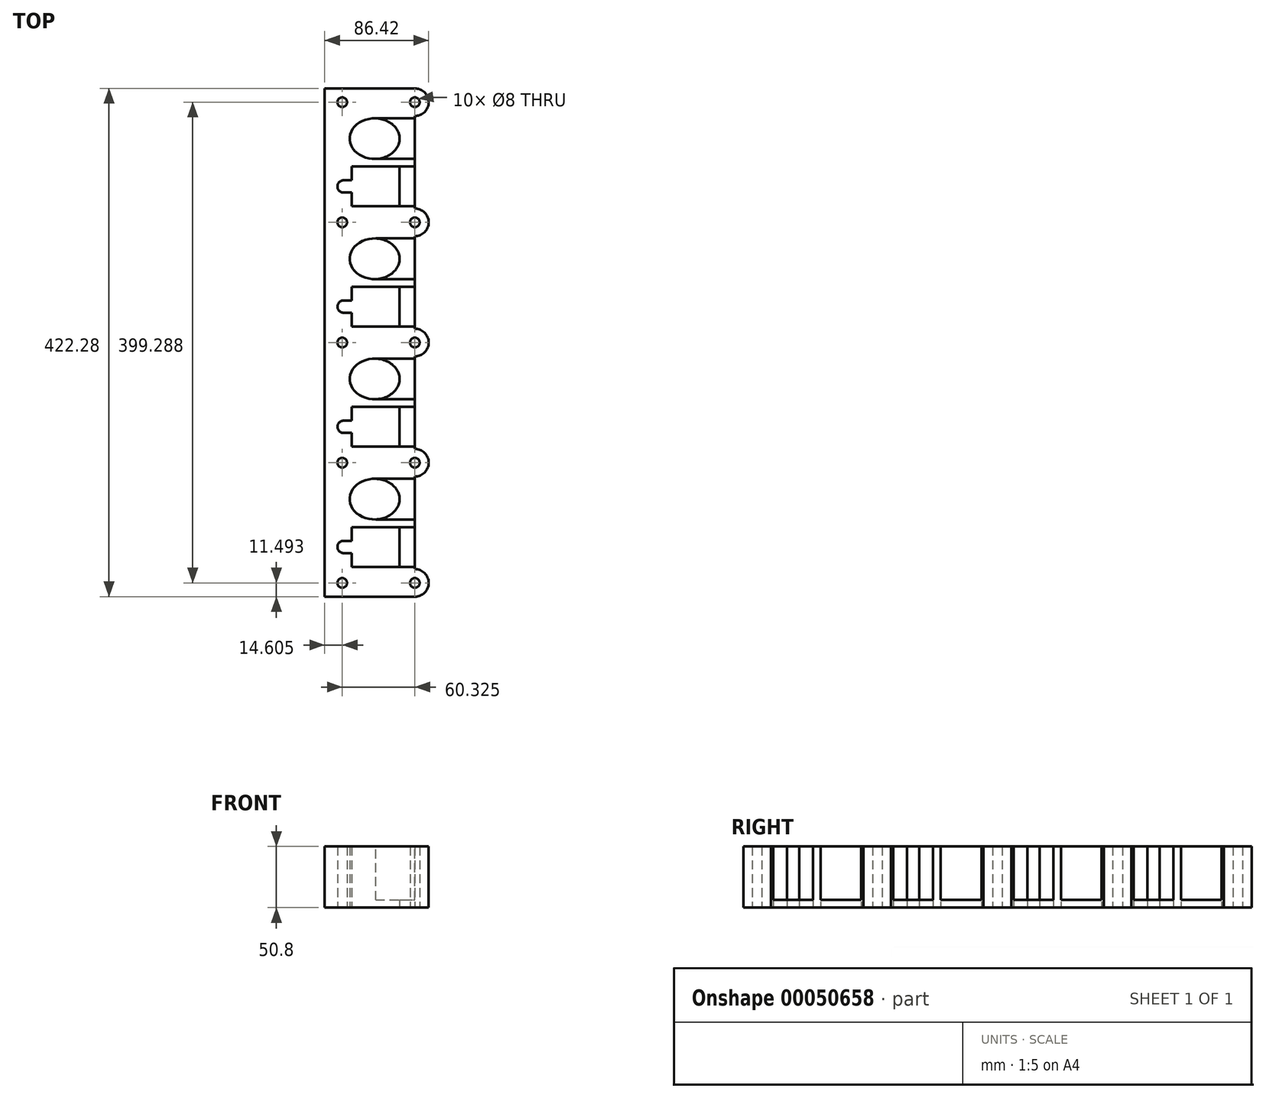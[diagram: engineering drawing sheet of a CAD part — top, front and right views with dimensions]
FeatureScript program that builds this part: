
annotation { "Feature Type Name" : "Feature", "Feature Type Description" : "" }
export const myFeature = defineFeature(function(context is Context, id is Id, definition is map)
    precondition{}
    {
        {
            var Q0;
            Q0=qCreatedBy(makeId("Top.planeOp"),FACE);
            var sketch = newSketch(context, id + "F0", { "sketchPlane" : qUnion([Q0])});
            skLineSegment(sketch, "E0.bottom", {"start": v(-7.62, 422.27) * mm, "end": v(-82.55, 422.27) * mm});
            skLineSegment(sketch, "E0.top", {"start": v(-7.62, 0) * mm, "end": v(-82.55, 0) * mm});
            skLineSegment(sketch, "E0.right", {"start": v(-82.55, 422.28) * mm, "end": v(-82.55, 0) * mm});
            skEllipse(sketch, "E1", {"center": v(-41.02, 81.09) * mm, "majorRadius": 20.7 * mm, "minorRadius": 16.9 * mm, "majorAxis": v(1, 0)});
            skLineSegment(sketch, "E2.bottom", {"start": v(-20.32, 57.85) * mm, "end": v(-59.94, 57.85) * mm});
            skLineSegment(sketch, "E2.top", {"start": v(-20.32, 24.83) * mm, "end": v(-59.94, 24.83) * mm});
            skLineSegment(sketch, "E2.left", {"start": v(-20.32, 57.85) * mm, "end": v(-20.32, 24.83) * mm});
            skLineSegment(sketch, "E2.right", {"start": v(-59.94, 57.85) * mm, "end": v(-59.94, 46.42) * mm});
            skLineSegment(sketch, "E3.bottom", {"start": v(-59.94, 46.42) * mm, "end": v(-66.8, 46.42) * mm});
            skLineSegment(sketch, "E3.top", {"start": v(-59.94, 36.26) * mm, "end": v(-66.8, 36.26) * mm});
            skArc(sketch, "E4", {"start": v(-66.8, 46.42) * mm, "mid": v(-71.88, 41.34) * mm, "end": v(-66.8, 36.26) * mm});
            skLineSegment(sketch, "E5.trimOffspring", {"start": v(-59.94, 36.26) * mm, "end": v(-59.94, 24.83) * mm});
            skPoint(sketch, "E6", {"position": v(-41.02, 64.2) * mm});
            skPoint(sketch, "E7", {"position": v(-20.32, 81.09) * mm});
            skPoint(sketch, "E8", {"position": v(-41.02, 97.98) * mm});
            skPoint(sketch, "E9.0.1.0", {"position": v(-41.02, 164.02) * mm});
            skPoint(sketch, "E9.0.1.1", {"position": v(-20.32, 180.91) * mm});
            skLineSegment(sketch, "E9.0.1.2", {"start": v(-20.32, 157.67) * mm, "end": v(-20.32, 124.65) * mm});
            skPoint(sketch, "E9.0.1.3", {"position": v(-41.02, 197.8) * mm});
            skLineSegment(sketch, "E9.0.1.4", {"start": v(-59.94, 136.08) * mm, "end": v(-66.8, 136.08) * mm});
            skLineSegment(sketch, "E9.0.1.5", {"start": v(-59.94, 157.67) * mm, "end": v(-59.94, 146.24) * mm});
            skLineSegment(sketch, "E9.0.1.6", {"start": v(-59.94, 146.24) * mm, "end": v(-66.8, 146.24) * mm});
            skEllipse(sketch, "E9.0.1.7", {"center": v(-41.02, 180.91) * mm, "majorRadius": 20.7 * mm, "minorRadius": 16.9 * mm, "majorAxis": v(1, 0)});
            skLineSegment(sketch, "E9.0.1.8", {"start": v(-59.94, 136.08) * mm, "end": v(-59.94, 124.65) * mm});
            skLineSegment(sketch, "E9.0.1.9", {"start": v(-20.32, 124.65) * mm, "end": v(-59.94, 124.65) * mm});
            skLineSegment(sketch, "E9.0.1.10", {"start": v(-20.32, 157.67) * mm, "end": v(-59.94, 157.67) * mm});
            skArc(sketch, "E9.0.1.11", {"start": v(-66.8, 146.24) * mm, "mid": v(-71.88, 141.16) * mm, "end": v(-66.8, 136.08) * mm});
            skPoint(sketch, "E9.0.2.0", {"position": v(-41.02, 263.84) * mm});
            skPoint(sketch, "E9.0.2.1", {"position": v(-20.32, 280.73) * mm});
            skLineSegment(sketch, "E9.0.2.2", {"start": v(-20.32, 257.5) * mm, "end": v(-20.32, 224.47) * mm});
            skPoint(sketch, "E9.0.2.3", {"position": v(-41.02, 297.62) * mm});
            skLineSegment(sketch, "E9.0.2.4", {"start": v(-59.94, 235.9) * mm, "end": v(-66.8, 235.9) * mm});
            skLineSegment(sketch, "E9.0.2.5", {"start": v(-59.94, 257.5) * mm, "end": v(-59.94, 246.06) * mm});
            skLineSegment(sketch, "E9.0.2.6", {"start": v(-59.94, 246.06) * mm, "end": v(-66.8, 246.06) * mm});
            skEllipse(sketch, "E9.0.2.7", {"center": v(-41.02, 280.73) * mm, "majorRadius": 20.7 * mm, "minorRadius": 16.9 * mm, "majorAxis": v(1, 0)});
            skLineSegment(sketch, "E9.0.2.8", {"start": v(-59.94, 235.9) * mm, "end": v(-59.94, 224.47) * mm});
            skLineSegment(sketch, "E9.0.2.9", {"start": v(-20.32, 224.47) * mm, "end": v(-59.94, 224.47) * mm});
            skLineSegment(sketch, "E9.0.2.10", {"start": v(-20.32, 257.5) * mm, "end": v(-59.94, 257.5) * mm});
            skArc(sketch, "E9.0.2.11", {"start": v(-66.8, 246.06) * mm, "mid": v(-71.88, 240.98) * mm, "end": v(-66.8, 235.9) * mm});
            skPoint(sketch, "E9.0.3.0", {"position": v(-41.02, 363.66) * mm});
            skPoint(sketch, "E9.0.3.1", {"position": v(-20.32, 380.56) * mm});
            skLineSegment(sketch, "E9.0.3.2", {"start": v(-20.32, 357.31) * mm, "end": v(-20.32, 324.3) * mm});
            skPoint(sketch, "E9.0.3.3", {"position": v(-41.02, 397.45) * mm});
            skLineSegment(sketch, "E9.0.3.4", {"start": v(-59.94, 335.72) * mm, "end": v(-66.8, 335.72) * mm});
            skLineSegment(sketch, "E9.0.3.5", {"start": v(-59.94, 357.31) * mm, "end": v(-59.94, 345.88) * mm});
            skLineSegment(sketch, "E9.0.3.6", {"start": v(-59.94, 345.88) * mm, "end": v(-66.8, 345.88) * mm});
            skEllipse(sketch, "E9.0.3.7", {"center": v(-41.02, 380.56) * mm, "majorRadius": 20.7 * mm, "minorRadius": 16.9 * mm, "majorAxis": v(1, 0)});
            skLineSegment(sketch, "E9.0.3.8", {"start": v(-59.94, 335.72) * mm, "end": v(-59.94, 324.3) * mm});
            skLineSegment(sketch, "E9.0.3.9", {"start": v(-20.32, 324.3) * mm, "end": v(-59.94, 324.3) * mm});
            skLineSegment(sketch, "E9.0.3.10", {"start": v(-20.32, 357.31) * mm, "end": v(-59.94, 357.31) * mm});
            skArc(sketch, "E9.0.3.11", {"start": v(-66.8, 345.88) * mm, "mid": v(-71.88, 340.8) * mm, "end": v(-66.8, 335.72) * mm});
            skLineSegment(sketch, "E9.direction1", {"start": v(-41.02, 64.2) * mm, "end": v(-15.62, 64.2) * mm, "construction": true});
            skLineSegment(sketch, "E9.direction2", {"start": v(-41.02, 64.2) * mm, "end": v(-41.02, 164.02) * mm, "construction": true});
            skLineSegment(sketch, "E10", {"start": v(-82.55, 11.5) * mm, "end": v(-19.11, 11.5) * mm, "construction": true});
            skLineSegment(sketch, "E11", {"start": v(-7.62, 11.5) * mm, "end": v(-7.62, 15.5) * mm, "construction": true});
            skLineSegment(sketch, "E12", {"start": v(-67.94, 422.27) * mm, "end": v(-67.94, 11.5) * mm, "construction": true});
            skLineSegment(sketch, "E13", {"start": v(-82.55, 364.1) * mm, "end": v(0, 364.1) * mm, "construction": true});
            skCircle(sketch, "E14", {"center": v(-7.62, 11.5) * mm, "radius": 4 * mm});
            skCircle(sketch, "E15", {"center": v(-67.94, 11.5) * mm, "radius": 4 * mm});
            skArc(sketch, "E16", {"start": v(-7.62, 0) * mm, "mid": v(3.87, 11.5) * mm, "end": v(-7.62, 22.99) * mm});
            skArc(sketch, "E17.0.1.0", {"start": v(-7.62, 99.82) * mm, "mid": v(3.87, 111.32) * mm, "end": v(-7.62, 122.8) * mm});
            skCircle(sketch, "E17.0.1.1", {"center": v(-7.62, 111.32) * mm, "radius": 4 * mm});
            skCircle(sketch, "E17.0.1.2", {"center": v(-67.94, 111.32) * mm, "radius": 4 * mm});
            skArc(sketch, "E17.0.2.0", {"start": v(-7.62, 199.64) * mm, "mid": v(3.87, 211.14) * mm, "end": v(-7.62, 222.63) * mm});
            skCircle(sketch, "E17.0.2.1", {"center": v(-7.62, 211.14) * mm, "radius": 4 * mm});
            skCircle(sketch, "E17.0.2.2", {"center": v(-67.94, 211.14) * mm, "radius": 4 * mm});
            skArc(sketch, "E17.0.3.0", {"start": v(-7.62, 299.47) * mm, "mid": v(3.87, 310.96) * mm, "end": v(-7.62, 322.45) * mm});
            skCircle(sketch, "E17.0.3.1", {"center": v(-7.62, 310.96) * mm, "radius": 4 * mm});
            skCircle(sketch, "E17.0.3.2", {"center": v(-67.94, 310.96) * mm, "radius": 4 * mm});
            skArc(sketch, "E17.0.4.0", {"start": v(-7.62, 399.29) * mm, "mid": v(3.87, 410.78) * mm, "end": v(-7.62, 422.27) * mm});
            skCircle(sketch, "E17.0.4.1", {"center": v(-7.62, 410.78) * mm, "radius": 4 * mm});
            skCircle(sketch, "E17.0.4.2", {"center": v(-67.94, 410.78) * mm, "radius": 4 * mm});
            skLineSegment(sketch, "E17.direction1", {"start": v(-7.62, 11.5) * mm, "end": v(11.43, 11.5) * mm, "construction": true});
            skLineSegment(sketch, "E18", {"start": v(-7.62, 399.29) * mm, "end": v(-7.62, 322.45) * mm});
            skLineSegment(sketch, "E19", {"start": v(-7.62, 222.63) * mm, "end": v(-7.62, 299.47) * mm});
            skLineSegment(sketch, "E20", {"start": v(-7.62, 199.64) * mm, "end": v(-7.62, 122.8) * mm});
            skLineSegment(sketch, "E21", {"start": v(-7.62, 99.82) * mm, "end": v(-7.62, 22.99) * mm});
            skLineSegment(sketch, "E22.trimOffspring", {"start": v(-7.62, 122.8) * mm, "end": v(-7.62, 422.27) * mm, "construction": true});
            skLineSegment(sketch, "E23.trimOffspring", {"start": v(0, 11.5) * mm, "end": v(0, 0) * mm});
            skLineSegment(sketch, "E24.trimOffspring", {"start": v(-7.62, 22.99) * mm, "end": v(-7.62, 99.82) * mm, "construction": true});
            skLineSegment(sketch, "E25.trimOffspring", {"start": v(-11.62, 11.5) * mm, "end": v(0, 11.5) * mm, "construction": true});
            skPoint(sketch, "E26.orphan", {"position": v(0, 422.28) * mm});
            skSolve(sketch);
        }
        {
            var Q0;
            Q0=makeQuery(id+"F0.imprint","IMPRINT",FACE,{"disambiguationData":[TD([[makeQuery(id+"F0.imprint","IMPRINT",EDGE,{"derivedFrom":sQuery(id+"F0.wireOp",EDGE,"E0.bottom")}),1.0]])]});
            extrude(context, id + "F1", {"entities" : qUnion([Q0]), "depth" : 50.8 * mm});
        }
        {
            var Q0;
            Q0=makeQuery(id+"F1.opExtrude","CAP_FACE",FACE,{"disambiguationData":[OSD([sQuery(id+"F0.wireOp",EDGE,"E0.bottom"),sQuery(id+"F0.wireOp",EDGE,"E0.top"),sQuery(id+"F0.wireOp",EDGE,"E0.right"),sQuery(id+"F0.wireOp",EDGE,"E1"),sQuery(id+"F0.wireOp",EDGE,"E2.bottom"),sQuery(id+"F0.wireOp",EDGE,"E2.top"),sQuery(id+"F0.wireOp",EDGE,"E2.left"),sQuery(id+"F0.wireOp",EDGE,"E2.right"),sQuery(id+"F0.wireOp",EDGE,"E3.bottom"),sQuery(id+"F0.wireOp",EDGE,"E3.top"),sQuery(id+"F0.wireOp",EDGE,"E4"),sQuery(id+"F0.wireOp",EDGE,"E5.trimOffspring"),sQuery(id+"F0.wireOp",EDGE,"E9.0.1.2"),sQuery(id+"F0.wireOp",EDGE,"E9.0.1.4"),sQuery(id+"F0.wireOp",EDGE,"E9.0.1.5"),sQuery(id+"F0.wireOp",EDGE,"E9.0.1.6"),sQuery(id+"F0.wireOp",EDGE,"E9.0.1.7"),sQuery(id+"F0.wireOp",EDGE,"E9.0.1.8"),sQuery(id+"F0.wireOp",EDGE,"E9.0.1.9"),sQuery(id+"F0.wireOp",EDGE,"E9.0.1.10"),sQuery(id+"F0.wireOp",EDGE,"E9.0.1.11"),sQuery(id+"F0.wireOp",EDGE,"E9.0.2.2"),sQuery(id+"F0.wireOp",EDGE,"E9.0.2.4"),sQuery(id+"F0.wireOp",EDGE,"E9.0.2.5"),sQuery(id+"F0.wireOp",EDGE,"E9.0.2.6"),sQuery(id+"F0.wireOp",EDGE,"E9.0.2.7"),sQuery(id+"F0.wireOp",EDGE,"E9.0.2.8"),sQuery(id+"F0.wireOp",EDGE,"E9.0.2.9"),sQuery(id+"F0.wireOp",EDGE,"E9.0.2.10"),sQuery(id+"F0.wireOp",EDGE,"E9.0.2.11"),sQuery(id+"F0.wireOp",EDGE,"E9.0.3.2"),sQuery(id+"F0.wireOp",EDGE,"E9.0.3.4"),sQuery(id+"F0.wireOp",EDGE,"E9.0.3.5"),sQuery(id+"F0.wireOp",EDGE,"E9.0.3.6"),sQuery(id+"F0.wireOp",EDGE,"E9.0.3.7"),sQuery(id+"F0.wireOp",EDGE,"E9.0.3.8"),sQuery(id+"F0.wireOp",EDGE,"E9.0.3.9"),sQuery(id+"F0.wireOp",EDGE,"E9.0.3.10"),sQuery(id+"F0.wireOp",EDGE,"E9.0.3.11"),sQuery(id+"F0.wireOp",EDGE,"E14"),sQuery(id+"F0.wireOp",EDGE,"E15"),sQuery(id+"F0.wireOp",EDGE,"E16"),sQuery(id+"F0.wireOp",EDGE,"E17.0.1.0"),sQuery(id+"F0.wireOp",EDGE,"E17.0.1.1"),sQuery(id+"F0.wireOp",EDGE,"E17.0.1.2"),sQuery(id+"F0.wireOp",EDGE,"E17.0.2.0"),sQuery(id+"F0.wireOp",EDGE,"E17.0.2.1"),sQuery(id+"F0.wireOp",EDGE,"E17.0.2.2"),sQuery(id+"F0.wireOp",EDGE,"E17.0.3.0"),sQuery(id+"F0.wireOp",EDGE,"E17.0.3.1"),sQuery(id+"F0.wireOp",EDGE,"E17.0.3.2"),sQuery(id+"F0.wireOp",EDGE,"E17.0.4.0"),sQuery(id+"F0.wireOp",EDGE,"E17.0.4.1"),sQuery(id+"F0.wireOp",EDGE,"E17.0.4.2"),sQuery(id+"F0.wireOp",EDGE,"E18"),sQuery(id+"F0.wireOp",EDGE,"E19"),sQuery(id+"F0.wireOp",EDGE,"E20"),sQuery(id+"F0.wireOp",EDGE,"E21")])],"isStart":false});
            var sketch = newSketch(context, id + "F2", { "sketchPlane" : qUnion([Q0])});
            skCircle(sketch, "E27", {"center": v(-66.8, 41.34) * mm, "radius": 12.7 * mm});
            skCircle(sketch, "E28", {"center": v(-66.8, 141.16) * mm, "radius": 12.7 * mm});
            skCircle(sketch, "E29", {"center": v(-66.8, 240.98) * mm, "radius": 12.7 * mm});
            skCircle(sketch, "E30", {"center": v(-66.8, 340.8) * mm, "radius": 12.7 * mm});
            skSolve(sketch);
        }
        {
            var Q0;
            Q0=makeQuery(id+"F2.imprint","IMPRINT",FACE,{"disambiguationData":[TD([[makeQuery(id+"F2.imprint","IMPRINT",EDGE,{"derivedFrom":makeQuery(id+"F1.opExtrude","CAP_EDGE",EDGE,{"disambiguationData":[OSD([sQuery(id+"F0.wireOp",EDGE,"E0.bottom")])],"isStart":false})}),1.0]])]});
            var sketch = newSketch(context, id + "F3", { "sketchPlane" : qUnion([Q0])});
            skPoint(sketch, "E31", {"position": v(-40.13, 97.96) * mm});
            skPoint(sketch, "E32", {"position": v(-40.13, 64.21) * mm});
            skPoint(sketch, "E33", {"position": v(-40.13, 57.85) * mm});
            skLineSegment(sketch, "E34", {"start": v(-40.13, 57.85) * mm, "end": v(-40.13, 99.27) * mm, "construction": true});
            skLineSegment(sketch, "E35.bottom", {"start": v(-40.13, 97.96) * mm, "end": v(-7.62, 97.96) * mm});
            skLineSegment(sketch, "E35.top", {"start": v(-40.13, 64.21) * mm, "end": v(-7.62, 64.21) * mm});
            skLineSegment(sketch, "E35.left", {"start": v(-40.13, 97.96) * mm, "end": v(-40.13, 64.21) * mm});
            skLineSegment(sketch, "E35.right", {"start": v(-7.62, 97.96) * mm, "end": v(-7.62, 64.21) * mm});
            skLineSegment(sketch, "E36.bottom", {"start": v(-40.13, 57.85) * mm, "end": v(-7.62, 57.85) * mm});
            skLineSegment(sketch, "E36.top", {"start": v(-40.13, 24.83) * mm, "end": v(-7.62, 24.83) * mm});
            skLineSegment(sketch, "E36.left", {"start": v(-40.13, 57.85) * mm, "end": v(-40.13, 24.83) * mm});
            skLineSegment(sketch, "E36.right", {"start": v(-7.62, 57.85) * mm, "end": v(-7.62, 24.83) * mm});
            skPoint(sketch, "E37.0.1.0", {"position": v(-40.13, 157.67) * mm});
            skLineSegment(sketch, "E37.0.1.1", {"start": v(-40.13, 157.67) * mm, "end": v(-7.62, 157.67) * mm});
            skLineSegment(sketch, "E37.0.1.2", {"start": v(-40.13, 124.65) * mm, "end": v(-7.62, 124.65) * mm});
            skLineSegment(sketch, "E37.0.1.3", {"start": v(-40.13, 157.67) * mm, "end": v(-40.13, 124.65) * mm});
            skLineSegment(sketch, "E37.0.1.4", {"start": v(-7.62, 157.67) * mm, "end": v(-7.62, 124.65) * mm});
            skLineSegment(sketch, "E37.0.1.5", {"start": v(-7.62, 197.79) * mm, "end": v(-7.62, 164.04) * mm});
            skLineSegment(sketch, "E37.0.1.6", {"start": v(-40.13, 197.79) * mm, "end": v(-40.13, 164.04) * mm});
            skLineSegment(sketch, "E37.0.1.7", {"start": v(-40.13, 164.04) * mm, "end": v(-7.62, 164.04) * mm});
            skLineSegment(sketch, "E37.0.1.8", {"start": v(-40.13, 197.79) * mm, "end": v(-7.62, 197.79) * mm});
            skPoint(sketch, "E37.0.1.9", {"position": v(-40.13, 197.79) * mm});
            skPoint(sketch, "E37.0.1.10", {"position": v(-40.13, 164.04) * mm});
            skLineSegment(sketch, "E37.0.1.11", {"start": v(-40.13, 157.67) * mm, "end": v(-40.13, 199.1) * mm, "construction": true});
            skPoint(sketch, "E37.0.2.0", {"position": v(-40.13, 257.5) * mm});
            skLineSegment(sketch, "E37.0.2.1", {"start": v(-40.13, 257.5) * mm, "end": v(-7.62, 257.5) * mm});
            skLineSegment(sketch, "E37.0.2.2", {"start": v(-40.13, 224.47) * mm, "end": v(-7.62, 224.47) * mm});
            skLineSegment(sketch, "E37.0.2.3", {"start": v(-40.13, 257.5) * mm, "end": v(-40.13, 224.47) * mm});
            skLineSegment(sketch, "E37.0.2.4", {"start": v(-7.62, 257.5) * mm, "end": v(-7.62, 224.47) * mm});
            skLineSegment(sketch, "E37.0.2.5", {"start": v(-7.62, 297.6) * mm, "end": v(-7.62, 263.86) * mm});
            skLineSegment(sketch, "E37.0.2.6", {"start": v(-40.13, 297.6) * mm, "end": v(-40.13, 263.86) * mm});
            skLineSegment(sketch, "E37.0.2.7", {"start": v(-40.13, 263.86) * mm, "end": v(-7.62, 263.86) * mm});
            skLineSegment(sketch, "E37.0.2.8", {"start": v(-40.13, 297.6) * mm, "end": v(-7.62, 297.6) * mm});
            skPoint(sketch, "E37.0.2.9", {"position": v(-40.13, 297.6) * mm});
            skPoint(sketch, "E37.0.2.10", {"position": v(-40.13, 263.86) * mm});
            skLineSegment(sketch, "E37.0.2.11", {"start": v(-40.13, 257.5) * mm, "end": v(-40.13, 298.92) * mm, "construction": true});
            skPoint(sketch, "E37.0.3.0", {"position": v(-40.13, 357.31) * mm});
            skLineSegment(sketch, "E37.0.3.1", {"start": v(-40.13, 357.31) * mm, "end": v(-7.62, 357.31) * mm});
            skLineSegment(sketch, "E37.0.3.2", {"start": v(-40.13, 324.3) * mm, "end": v(-7.62, 324.3) * mm});
            skLineSegment(sketch, "E37.0.3.3", {"start": v(-40.13, 357.31) * mm, "end": v(-40.13, 324.3) * mm});
            skLineSegment(sketch, "E37.0.3.4", {"start": v(-7.62, 357.31) * mm, "end": v(-7.62, 324.3) * mm});
            skLineSegment(sketch, "E37.0.3.5", {"start": v(-7.62, 397.43) * mm, "end": v(-7.62, 363.68) * mm});
            skLineSegment(sketch, "E37.0.3.6", {"start": v(-40.13, 397.43) * mm, "end": v(-40.13, 363.68) * mm});
            skLineSegment(sketch, "E37.0.3.7", {"start": v(-40.13, 363.68) * mm, "end": v(-7.62, 363.68) * mm});
            skLineSegment(sketch, "E37.0.3.8", {"start": v(-40.13, 397.43) * mm, "end": v(-7.62, 397.43) * mm});
            skPoint(sketch, "E37.0.3.9", {"position": v(-40.13, 397.43) * mm});
            skPoint(sketch, "E37.0.3.10", {"position": v(-40.13, 363.68) * mm});
            skLineSegment(sketch, "E37.0.3.11", {"start": v(-40.13, 357.31) * mm, "end": v(-40.13, 398.74) * mm, "construction": true});
            skLineSegment(sketch, "E37.direction1", {"start": v(-40.13, 57.85) * mm, "end": v(-14.73, 57.85) * mm, "construction": true});
            skLineSegment(sketch, "E37.direction2", {"start": v(-40.13, 57.85) * mm, "end": v(-40.13, 157.67) * mm, "construction": true});
            skSolve(sketch);
        }
        {
            var Q0;
            Q0 = qSketchRegion(id + "F3", true);
            extrude(context, id + "F4", {"entities" : qUnion([Q0]), "operationType" : NewBodyOperationType.REMOVE, "oppositeDirection" : true, "depth" : 44.45 * mm});
        }
    });
